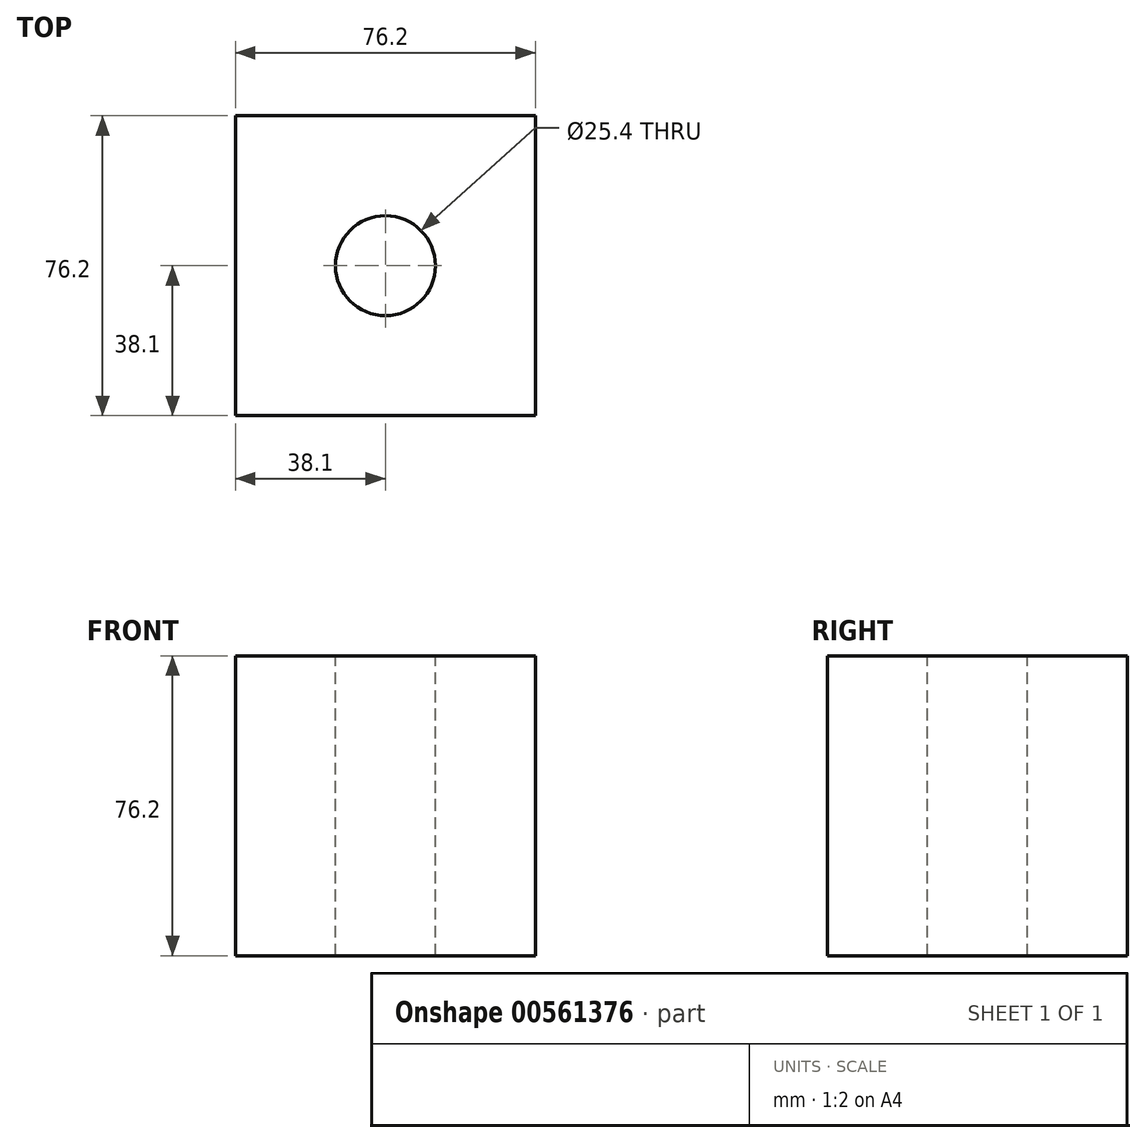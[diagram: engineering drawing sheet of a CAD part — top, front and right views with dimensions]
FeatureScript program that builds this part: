
annotation { "Feature Type Name" : "Feature", "Feature Type Description" : "" }
export const myFeature = defineFeature(function(context is Context, id is Id, definition is map)
    precondition{}
    {
        {
            var Q0;
            Q0=qCreatedBy(makeId("Front.planeOp"),FACE);
            var sketch = newSketch(context, id + "F0", { "sketchPlane" : qUnion([Q0])});
            skLineSegment(sketch, "E0.bottom", {"start": v(0, 0) * mm, "end": v(-76.2, 0) * mm});
            skLineSegment(sketch, "E0.top", {"start": v(0, 76.2) * mm, "end": v(-76.2, 76.2) * mm});
            skLineSegment(sketch, "E0.left", {"start": v(0, 0) * mm, "end": v(0, 76.2) * mm});
            skLineSegment(sketch, "E0.right", {"start": v(-76.2, 0) * mm, "end": v(-76.2, 76.2) * mm});
            skSolve(sketch);
        }
        {
            var Q0;
            Q0=makeQuery(id+"F0.imprint","IMPRINT",FACE,{"disambiguationData":[TD([[makeQuery(id+"F0.imprint","IMPRINT",EDGE,{"derivedFrom":sQuery(id+"F0.wireOp",EDGE,"E0.bottom")}),-1.0]])]});
            extrude(context, id + "F1", {"entities" : qUnion([Q0]), "depth" : 76.2 * mm, "offsetDistance" : 25.4 * mm});
        }
        {
            var Q0;
            Q0=makeQuery(id+"F1.opExtrude","SWEPT_FACE",FACE,{"disambiguationData":[OSD([sQuery(id+"F0.wireOp",EDGE,"E0.top")])]});
            var sketch = newSketch(context, id + "F2", { "sketchPlane" : qUnion([Q0])});
            skCircle(sketch, "E1", {"center": v(-38.1, -38.1) * mm, "radius": 12.7 * mm});
            skSolve(sketch);
        }
        {
            var Q0;
            Q0=sQuery(id+"F2.wireOp",VERTEX,"E1.center");
            var Q1;
            Q1=makeQuery(id+"F1.opExtrude","SWEPT_BODY",BODY,{"disambiguationData":[OSD([sQuery(id+"F0.wireOp",EDGE,"E0.bottom"),sQuery(id+"F0.wireOp",EDGE,"E0.top"),sQuery(id+"F0.wireOp",EDGE,"E0.left"),sQuery(id+"F0.wireOp",EDGE,"E0.right")])]});
            hole(context, id + "F3", {"style" : HoleStyle.SIMPLE, "endStyle" : HoleEndStyle.THROUGH, "holeDiameter" : 25.4 * mm, "isTappedThrough" : true, "tappedDepth" : 12.7 * mm, "tapClearance" : 3, "locations" : qUnion([Q0]), "scope" : qUnion([Q1])});
        }
    });
